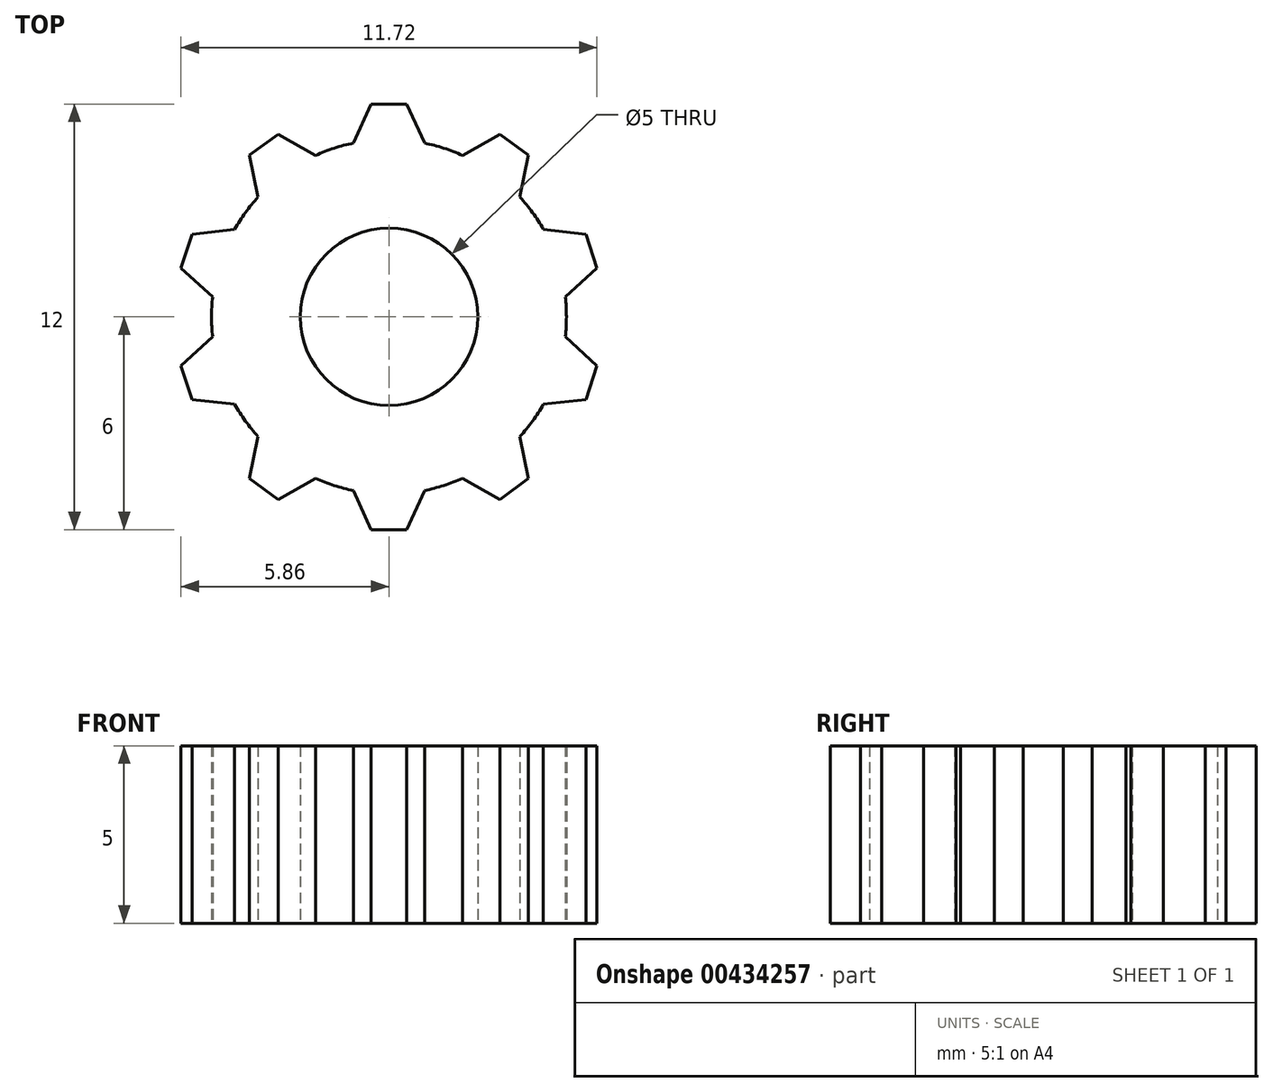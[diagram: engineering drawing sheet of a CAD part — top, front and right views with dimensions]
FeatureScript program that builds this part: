
annotation { "Feature Type Name" : "Feature", "Feature Type Description" : "" }
export const myFeature = defineFeature(function(context is Context, id is Id, definition is map)
    precondition{}
    {
        {
            var Q0;
            Q0=qCreatedBy(makeId("Top.planeOp"),FACE);
            var sketch = newSketch(context, id + "F0", { "sketchPlane" : qUnion([Q0])});
            skArc(sketch, "E0", {"start": v(-4.97, 0.56) * mm, "mid": v(-5, 0) * mm, "end": v(-4.97, -0.56) * mm});
            skLineSegment(sketch, "E1", {"start": v(1, 6) * mm, "end": v(1, 4.9) * mm, "construction": true});
            skLineSegment(sketch, "E2.MirrorCS", {"start": v(-1, 6) * mm, "end": v(-1, 4.9) * mm, "construction": true});
            skLineSegment(sketch, "E3", {"start": v(-1, 4.9) * mm, "end": v(-0.5, 6) * mm});
            skLineSegment(sketch, "E4", {"start": v(-0.5, 6) * mm, "end": v(0.5, 6) * mm});
            skLineSegment(sketch, "E5", {"start": v(0.5, 6) * mm, "end": v(1, 4.9) * mm});
            skLineSegment(sketch, "E6.1.0", {"start": v(-3.69, 3.38) * mm, "end": v(-3.93, 4.56) * mm});
            skLineSegment(sketch, "E6.1.1", {"start": v(-3.93, 4.56) * mm, "end": v(-3.12, 5.15) * mm});
            skLineSegment(sketch, "E6.1.2", {"start": v(-3.12, 5.15) * mm, "end": v(-2.07, 4.55) * mm});
            skLineSegment(sketch, "E6.2.0", {"start": v(-4.97, 0.56) * mm, "end": v(-5.86, 1.38) * mm});
            skLineSegment(sketch, "E6.2.1", {"start": v(-5.86, 1.38) * mm, "end": v(-5.55, 2.33) * mm});
            skLineSegment(sketch, "E6.2.2", {"start": v(-5.55, 2.33) * mm, "end": v(-4.35, 2.46) * mm});
            skLineSegment(sketch, "E6.3.0", {"start": v(-4.35, -2.46) * mm, "end": v(-5.55, -2.33) * mm});
            skLineSegment(sketch, "E6.3.1", {"start": v(-5.55, -2.33) * mm, "end": v(-5.86, -1.38) * mm});
            skLineSegment(sketch, "E6.3.2", {"start": v(-5.86, -1.38) * mm, "end": v(-4.97, -0.56) * mm});
            skLineSegment(sketch, "E6.4.0", {"start": v(-2.07, -4.55) * mm, "end": v(-3.12, -5.15) * mm});
            skLineSegment(sketch, "E6.4.1", {"start": v(-3.12, -5.15) * mm, "end": v(-3.93, -4.56) * mm});
            skLineSegment(sketch, "E6.4.2", {"start": v(-3.93, -4.56) * mm, "end": v(-3.69, -3.38) * mm});
            skLineSegment(sketch, "E6.5.0", {"start": v(1, -4.9) * mm, "end": v(0.5, -6) * mm});
            skLineSegment(sketch, "E6.5.1", {"start": v(0.5, -6) * mm, "end": v(-0.5, -6) * mm});
            skLineSegment(sketch, "E6.5.2", {"start": v(-0.5, -6) * mm, "end": v(-1, -4.9) * mm});
            skLineSegment(sketch, "E6.6.0", {"start": v(3.69, -3.38) * mm, "end": v(3.93, -4.56) * mm});
            skLineSegment(sketch, "E6.6.1", {"start": v(3.93, -4.56) * mm, "end": v(3.12, -5.15) * mm});
            skLineSegment(sketch, "E6.6.2", {"start": v(3.12, -5.15) * mm, "end": v(2.07, -4.55) * mm});
            skLineSegment(sketch, "E6.7.0", {"start": v(4.97, -0.56) * mm, "end": v(5.86, -1.38) * mm});
            skLineSegment(sketch, "E6.7.1", {"start": v(5.86, -1.38) * mm, "end": v(5.55, -2.33) * mm});
            skLineSegment(sketch, "E6.7.2", {"start": v(5.55, -2.33) * mm, "end": v(4.35, -2.46) * mm});
            skLineSegment(sketch, "E6.8.0", {"start": v(4.35, 2.46) * mm, "end": v(5.55, 2.33) * mm});
            skLineSegment(sketch, "E6.8.1", {"start": v(5.55, 2.33) * mm, "end": v(5.86, 1.38) * mm});
            skLineSegment(sketch, "E6.8.2", {"start": v(5.86, 1.38) * mm, "end": v(4.97, 0.56) * mm});
            skLineSegment(sketch, "E6.9.0", {"start": v(2.07, 4.55) * mm, "end": v(3.12, 5.15) * mm});
            skLineSegment(sketch, "E6.9.1", {"start": v(3.12, 5.15) * mm, "end": v(3.93, 4.56) * mm});
            skLineSegment(sketch, "E6.9.2", {"start": v(3.93, 4.56) * mm, "end": v(3.69, 3.38) * mm});
            skArc(sketch, "E7.trimOffspring", {"start": v(-3.69, 3.38) * mm, "mid": v(-4.05, 2.94) * mm, "end": v(-4.35, 2.46) * mm});
            skArc(sketch, "E8.trimOffspring", {"start": v(-1, 4.9) * mm, "mid": v(-1.55, 4.76) * mm, "end": v(-2.07, 4.55) * mm});
            skArc(sketch, "E9.trimOffspring", {"start": v(2.07, 4.55) * mm, "mid": v(1.55, 4.76) * mm, "end": v(1, 4.9) * mm});
            skArc(sketch, "E10.trimOffspring", {"start": v(4.35, 2.46) * mm, "mid": v(4.05, 2.94) * mm, "end": v(3.69, 3.38) * mm});
            skArc(sketch, "E11.trimOffspring", {"start": v(4.97, -0.56) * mm, "mid": v(5, 0) * mm, "end": v(4.97, 0.56) * mm});
            skArc(sketch, "E12.trimOffspring", {"start": v(3.69, -3.38) * mm, "mid": v(4.05, -2.94) * mm, "end": v(4.35, -2.46) * mm});
            skArc(sketch, "E13.trimOffspring", {"start": v(1, -4.9) * mm, "mid": v(1.55, -4.76) * mm, "end": v(2.07, -4.55) * mm});
            skArc(sketch, "E14.trimOffspring", {"start": v(-2.07, -4.55) * mm, "mid": v(-1.55, -4.76) * mm, "end": v(-1, -4.9) * mm});
            skArc(sketch, "E15.trimOffspring", {"start": v(-4.35, -2.46) * mm, "mid": v(-4.05, -2.94) * mm, "end": v(-3.69, -3.38) * mm});
            skCircle(sketch, "E16", {"center": v(0, 0) * mm, "radius": 2.5 * mm});
            skSolve(sketch);
        }
        {
            var Q0;
            Q0=makeQuery(id+"F0.imprint","IMPRINT",FACE,{"disambiguationData":[TD([[makeQuery(id+"F0.imprint","IMPRINT",EDGE,{"derivedFrom":sQuery(id+"F0.wireOp",EDGE,"E0")}),1.0]])]});
            extrude(context, id + "F1", {"entities" : qUnion([Q0]), "depth" : 5 * mm});
        }
    });
